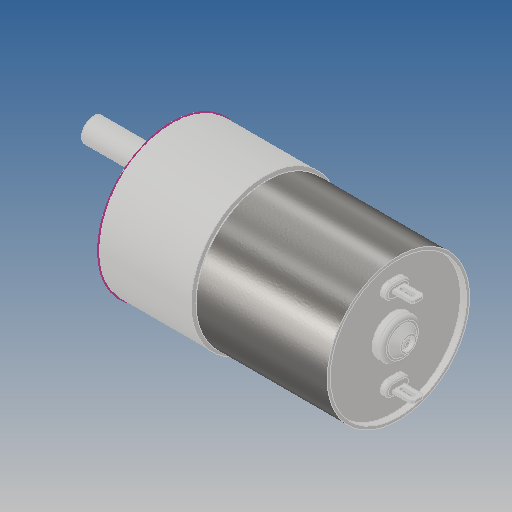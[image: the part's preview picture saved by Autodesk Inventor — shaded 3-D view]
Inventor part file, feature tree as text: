
AUTODESK INVENTOR PART (.ipt)
format: ipt  version: 2020 (Build 240168000, 168)  size: 295,936 bytes
history: native  units: mm
features: sketch x2, projected_geometry x2, extrude x1, other x1
ambient origin geometry x8: Origin, YZ Plane, XZ Plane, XY Plane, X Axis, Y Axis, Z Axis, Center Point
bodies: Solid1 (feature_tree)
feature tree (6):
  sketch  "Sketch1"  dims[d0=8.0mm d1=45.75mm d2=0.0mm]
  extrude  "Extrusion1"  Depth=45.75mm TaperAngle=0.0deg
  projected_geometry  "Projected Loop1"
  projected_geometry  "Projected Loop2"
  sketch  "Sketch2"
  other  "Aynalama2"
